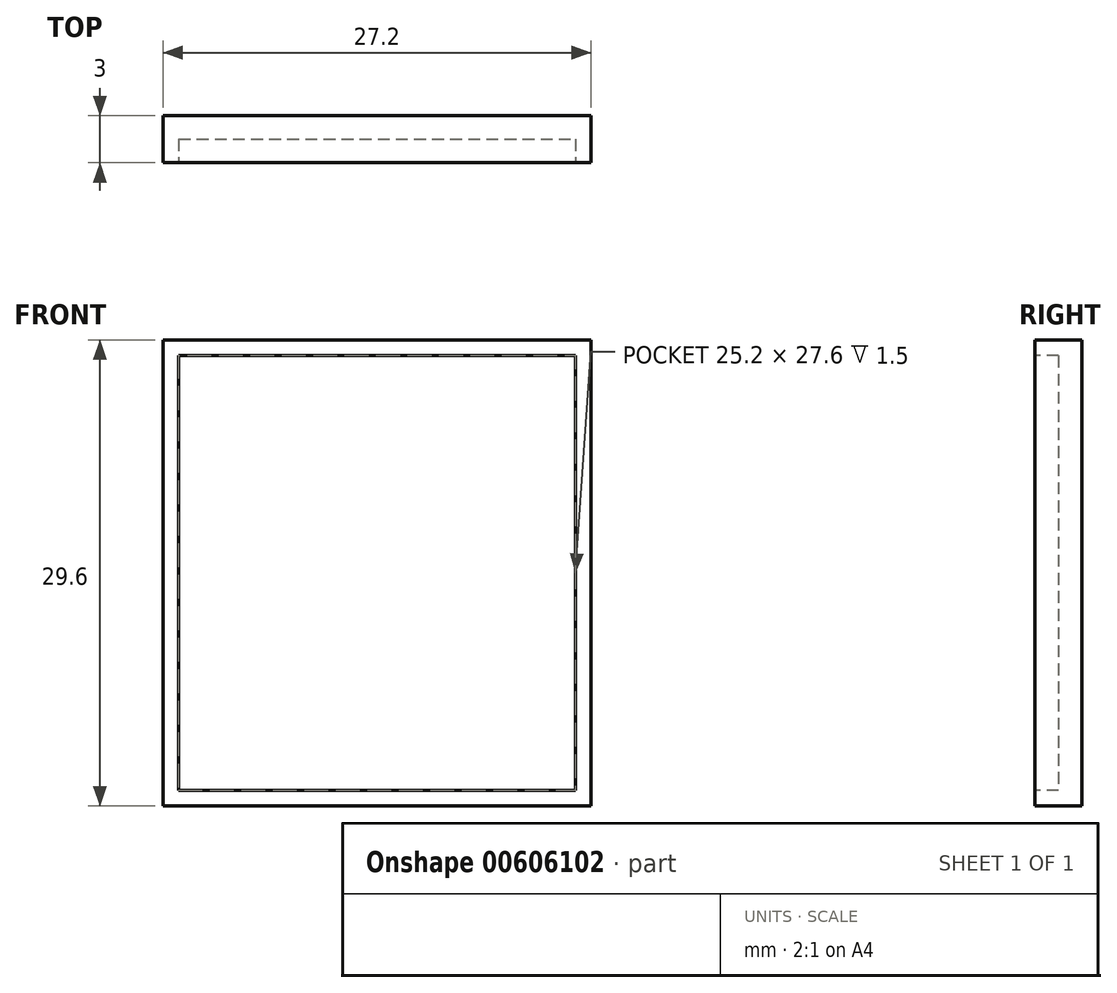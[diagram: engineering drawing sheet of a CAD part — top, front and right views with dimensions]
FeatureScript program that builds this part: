
annotation { "Feature Type Name" : "Feature", "Feature Type Description" : "" }
export const myFeature = defineFeature(function(context is Context, id is Id, definition is map)
    precondition{}
    {
        {
            var Q0;
            Q0=qCreatedBy(makeId("Front.planeOp"),FACE);
            var sketch = newSketch(context, id + "F0", { "sketchPlane" : qUnion([Q0])});
            skLineSegment(sketch, "E0.bottom", {"start": v(-13.6, 14.8) * mm, "end": v(13.6, 14.8) * mm});
            skLineSegment(sketch, "E0.top", {"start": v(-13.6, -14.8) * mm, "end": v(13.6, -14.8) * mm});
            skLineSegment(sketch, "E0.left", {"start": v(-13.6, 14.8) * mm, "end": v(-13.6, -14.8) * mm});
            skLineSegment(sketch, "E0.right", {"start": v(13.6, 14.8) * mm, "end": v(13.6, -14.8) * mm});
            skLineSegment(sketch, "E1", {"start": v(13.6, 14.8) * mm, "end": v(-13.6, -14.8) * mm, "construction": true});
            skSolve(sketch);
        }
        {
            var Q0;
            Q0 = qSketchRegion(id + "F0", true);
            extrude(context, id + "F1", {"entities" : qUnion([Q0]), "depth" : 3 * mm, "offsetDistance" : 25 * mm});
        }
        {
            var Q0;
            Q0=makeQuery(id+"F1.opExtrude","CAP_FACE",FACE,{"disambiguationData":[OSD([sQuery(id+"F0.wireOp",EDGE,"E0.bottom"),sQuery(id+"F0.wireOp",EDGE,"E0.top"),sQuery(id+"F0.wireOp",EDGE,"E0.left"),sQuery(id+"F0.wireOp",EDGE,"E0.right")])],"isStart":false});
            var sketch = newSketch(context, id + "F2", { "sketchPlane" : qUnion([Q0])});
            skLineSegment(sketch, "E2.0", {"start": v(-12.6, 13.8) * mm, "end": v(12.6, 13.8) * mm});
            skLineSegment(sketch, "E2.1", {"start": v(-12.6, 13.8) * mm, "end": v(-12.6, -13.8) * mm});
            skLineSegment(sketch, "E2.2", {"start": v(-12.6, -13.8) * mm, "end": v(12.6, -13.8) * mm});
            skLineSegment(sketch, "E2.3", {"start": v(12.6, 13.8) * mm, "end": v(12.6, -13.8) * mm});
            skSolve(sketch);
        }
        {
            var Q0;
            Q0 = qSketchRegion(id + "F2", true);
            extrude(context, id + "F3", {"entities" : qUnion([Q0]), "operationType" : NewBodyOperationType.REMOVE, "oppositeDirection" : true, "depth" : 1.5 * mm, "offsetDistance" : 25 * mm});
        }
    });
